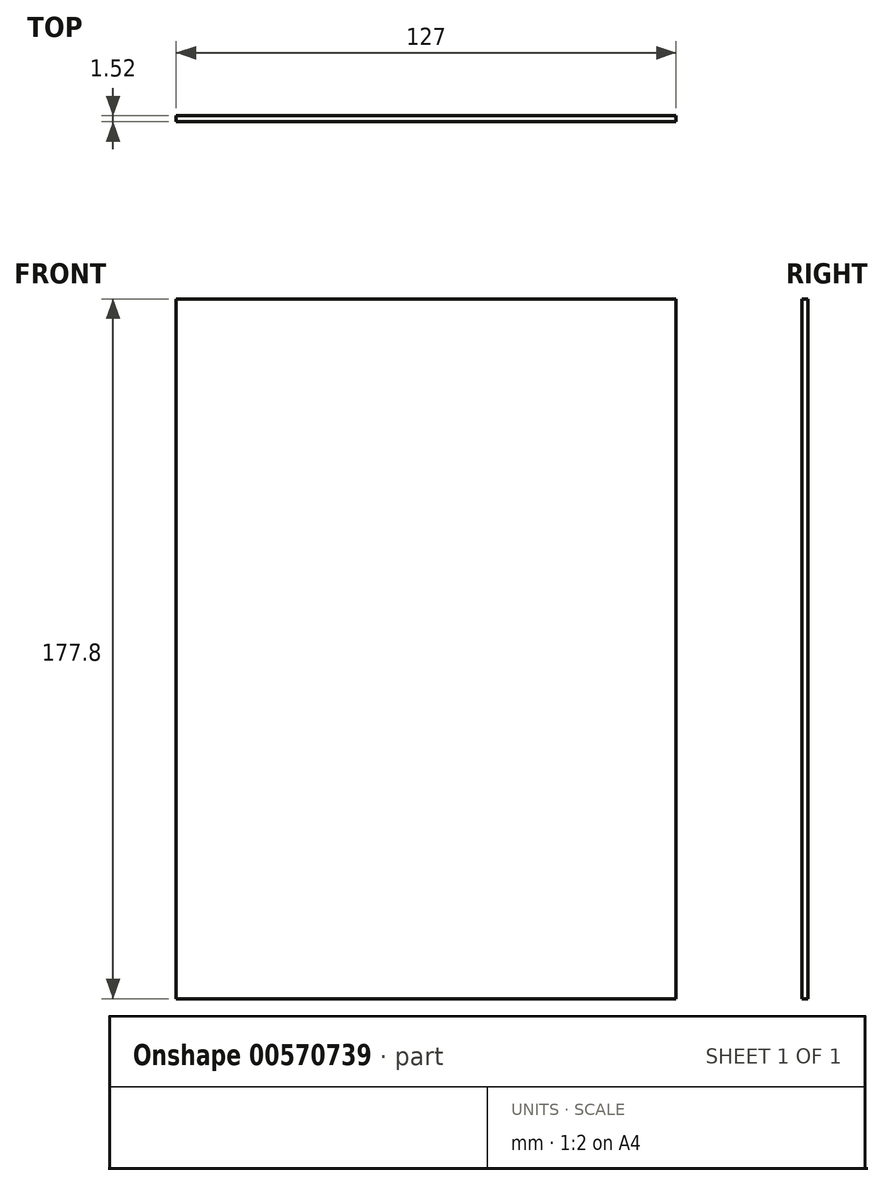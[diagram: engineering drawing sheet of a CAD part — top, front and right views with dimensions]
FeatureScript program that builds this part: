
annotation { "Feature Type Name" : "Feature", "Feature Type Description" : "" }
export const myFeature = defineFeature(function(context is Context, id is Id, definition is map)
    precondition{}
    {
        {
            var Q0;
            Q0=qCreatedBy(makeId("Front.planeOp"),FACE);
            var sketch = newSketch(context, id + "F0", { "sketchPlane" : qUnion([Q0])});
            skLineSegment(sketch, "E0.bottom", {"start": v(63.5, 88.9) * mm, "end": v(-63.5, 88.9) * mm});
            skLineSegment(sketch, "E0.top", {"start": v(63.5, -88.9) * mm, "end": v(-63.5, -88.9) * mm});
            skLineSegment(sketch, "E0.left", {"start": v(63.5, 88.9) * mm, "end": v(63.5, -88.9) * mm});
            skLineSegment(sketch, "E0.right", {"start": v(-63.5, 88.9) * mm, "end": v(-63.5, -88.9) * mm});
            skPoint(sketch, "E0.middle", {"position": v(0, 0) * mm});
            skSolve(sketch);
        }
        {
            var Q0;
            Q0=makeQuery(id+"F0.imprint","IMPRINT",FACE,{"disambiguationData":[TD([[makeQuery(id+"F0.imprint","IMPRINT",EDGE,{"derivedFrom":sQuery(id+"F0.wireOp",EDGE,"E0.bottom")}),1.0]])]});
            extrude(context, id + "F1", {"entities" : qUnion([Q0]), "endBound" : BoundingType.SYMMETRIC, "depth" : 1.52 * mm, "offsetDistance" : 25.4 * mm});
        }
    });
